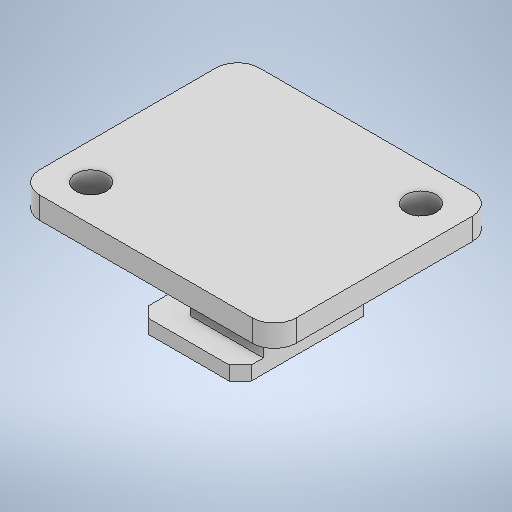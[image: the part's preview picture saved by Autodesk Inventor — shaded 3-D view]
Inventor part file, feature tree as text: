
AUTODESK INVENTOR PART (.ipt)
format: ipt  version: 2025.1 (Build 291241000, 241)  size: 276,992 bytes
history: native  units: mm
features: sketch x4, extrude x3, fillet x3, chamfer x1, hole x1
ambient origin geometry x8: Origin, YZ Plane, XZ Plane, XY Plane, X Axis, Y Axis, Z Axis, Center Point
bodies: Volumenkörper1 (feature_tree)
feature tree (12):
  extrude  "Extrusion1"  Depth=1.9mm
  chamfer  "Fasen1"  Distance=1.9mm
  extrude  "Extrusion2"  Depth=10.0mm
  extrude  "Extrusion3"  Depth=10.0mm TaperAngle=0.0deg
  hole  "Bohrung1"  [1 undecoded]
  fillet  "Rundung1"  Radius=3.0mm
  fillet  "Rundung2"  Radius=25.0mm
  fillet  "Rundung3"  Radius=20.0mm
  sketch  "Skizze1"  dims[d0=14.0mm d1=18.3mm d2=1.9mm d3=0.0mm]
  sketch  "Skizze2"  dims[d4=1.5mm d5=2.0mm d6=45.0deg d7=10.0mm]
  sketch  "Skizze3"  dims[d8=12.0mm d9=10.0mm d10=0.0mm]
  sketch  "Skizze4"  dims[d11=35.0mm d12=30.0mm d13=3.0mm d14=0.0mm d15=25.0mm d16=20.0mm d17=4.2mm d18=6.0mm d19=4.0mm d20=2.0mm d21=90.0deg d22=8.0mm d23=20.594885mm d24=5.0mm d25=3.0mm d26=3.0mm]
note: 1 required parameter value undecoded (feature->parameter linkage not recoverable at this tier; creation-order binding heuristic only, values carry confidence <= 0.55)
